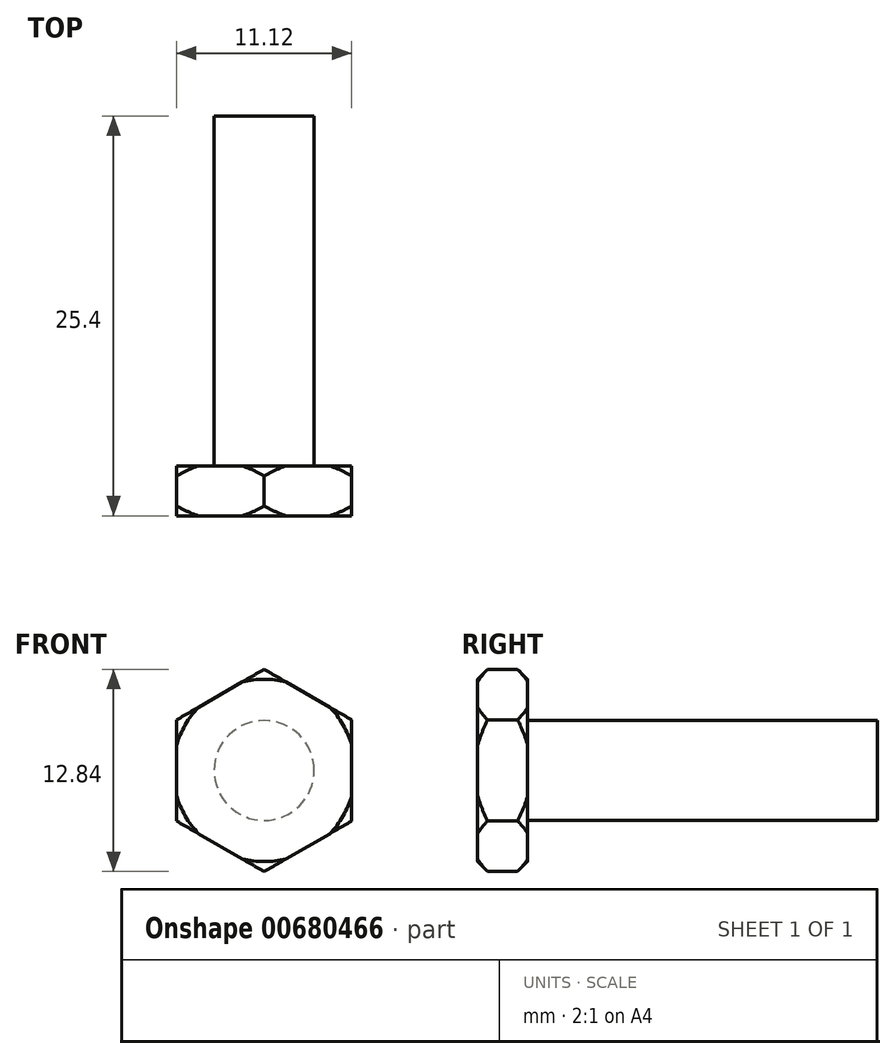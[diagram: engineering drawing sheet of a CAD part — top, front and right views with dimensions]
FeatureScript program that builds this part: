
annotation { "Feature Type Name" : "Feature", "Feature Type Description" : "" }
export const myFeature = defineFeature(function(context is Context, id is Id, definition is map)
    precondition{}
    {
        {
            var Q0;
            Q0=qCreatedBy(makeId("Front.planeOp"),FACE);
            var sketch = newSketch(context, id + "F0", { "sketchPlane" : qUnion([Q0])});
            skCircle(sketch, "E0", {"center": v(0, 0) * mm, "radius": 3.18 * mm});
            skSolve(sketch);
        }
        {
            var Q0;
            Q0=makeQuery(id+"F0.imprint","IMPRINT",FACE,{"disambiguationData":[TD([[makeQuery(id+"F0.imprint","IMPRINT",EDGE,{"derivedFrom":sQuery(id+"F0.wireOp",EDGE,"E0")}),1.0]])]});
            extrude(context, id + "F1", {"entities" : qUnion([Q0]), "depth" : 22.22 * mm, "offsetDistance" : 25.4 * mm});
        }
        {
            var Q0;
            Q0=makeQuery(id+"F1.opExtrude","CAP_FACE",FACE,{"disambiguationData":[OSD([sQuery(id+"F0.wireOp",EDGE,"E0")])],"isStart":false});
            var sketch = newSketch(context, id + "F2", { "sketchPlane" : qUnion([Q0])});
            skCircle(sketch, "E1.cCircle", {"center": v(0, 0) * mm, "radius": 5.56 * mm, "construction": true});
            skLineSegment(sketch, "E1.0", {"start": v(0, 6.42) * mm, "end": v(5.56, 3.21) * mm});
            skLineSegment(sketch, "E1.1", {"start": v(5.56, 3.21) * mm, "end": v(5.56, -3.21) * mm});
            skLineSegment(sketch, "E1.2", {"start": v(5.56, -3.21) * mm, "end": v(0, -6.42) * mm});
            skLineSegment(sketch, "E1.3", {"start": v(0, -6.42) * mm, "end": v(-5.56, -3.21) * mm});
            skLineSegment(sketch, "E1.4", {"start": v(-5.56, -3.21) * mm, "end": v(-5.56, 3.21) * mm});
            skLineSegment(sketch, "E1.5", {"start": v(-5.56, 3.21) * mm, "end": v(0, 6.42) * mm});
            skPoint(sketch, "E1.0.midPoint", {"position": v(2.78, 4.82) * mm});
            skSolve(sketch);
        }
        {
            var Q0;
            Q0=makeQuery(id+"F2.imprint","IMPRINT",FACE,{"disambiguationData":[TD([[makeQuery(id+"F2.imprint","IMPRINT",EDGE,{"derivedFrom":sQuery(id+"F2.wireOp",EDGE,"E1.0")}),-1.0]])]});
            var Q1;
            Q1=makeQuery(id+"F2.imprint","IMPRINT",FACE,{"disambiguationData":[TD([[makeQuery(id+"F2.imprint","IMPRINT",EDGE,{"derivedFrom":makeQuery(id+"F1.opExtrude","CAP_EDGE",EDGE,{"disambiguationData":[OSD([sQuery(id+"F0.wireOp",EDGE,"E0")])],"isStart":false})}),1.0]])]});
            extrude(context, id + "F3", {"entities" : qUnion([Q0, Q1]), "operationType" : NewBodyOperationType.ADD, "depth" : 3.17 * mm, "offsetDistance" : 25.4 * mm});
        }
        {
            var Q0;
            Q0=qCreatedBy(makeId("Right.planeOp"),FACE);
            var sketch = newSketch(context, id + "F4", { "sketchPlane" : qUnion([Q0])});
            skLineSegment(sketch, "E2", {"start": v(-25.4, 6.42) * mm, "end": v(-24.77, 6.42) * mm});
            skLineSegment(sketch, "E3", {"start": v(-24.77, 6.42) * mm, "end": v(-25.4, 5.79) * mm});
            skLineSegment(sketch, "E4", {"start": v(-25.4, 5.79) * mm, "end": v(-25.4, 6.42) * mm});
            skLineSegment(sketch, "E5", {"start": v(-23.81, 3.21) * mm, "end": v(-23.81, 1.19) * mm, "construction": true});
            skLineSegment(sketch, "E6.MirrorCS", {"start": v(-22.22, 6.42) * mm, "end": v(-22.86, 6.42) * mm});
            skLineSegment(sketch, "E7.MirrorCS", {"start": v(-22.22, 5.79) * mm, "end": v(-22.22, 6.42) * mm});
            skLineSegment(sketch, "E8.MirrorCS", {"start": v(-22.86, 6.42) * mm, "end": v(-22.22, 5.79) * mm});
            skSolve(sketch);
        }
        {
            var Q0;
            Q0 = qSketchRegion(id + "F4", true);
            var Q1;
            Q1=makeQuery(id+"F1.opExtrude","SWEPT_FACE",FACE,{"disambiguationData":[OSD([sQuery(id+"F0.wireOp",EDGE,"E0")])]});
            revolve(context, id + "F5", {"operationType" : NewBodyOperationType.REMOVE, "entities" : qUnion([Q0]), "axis" : qUnion([Q1]), "revolveType" : RevolveType.FULL, "oppositeDirection" : true});
        }
    });
